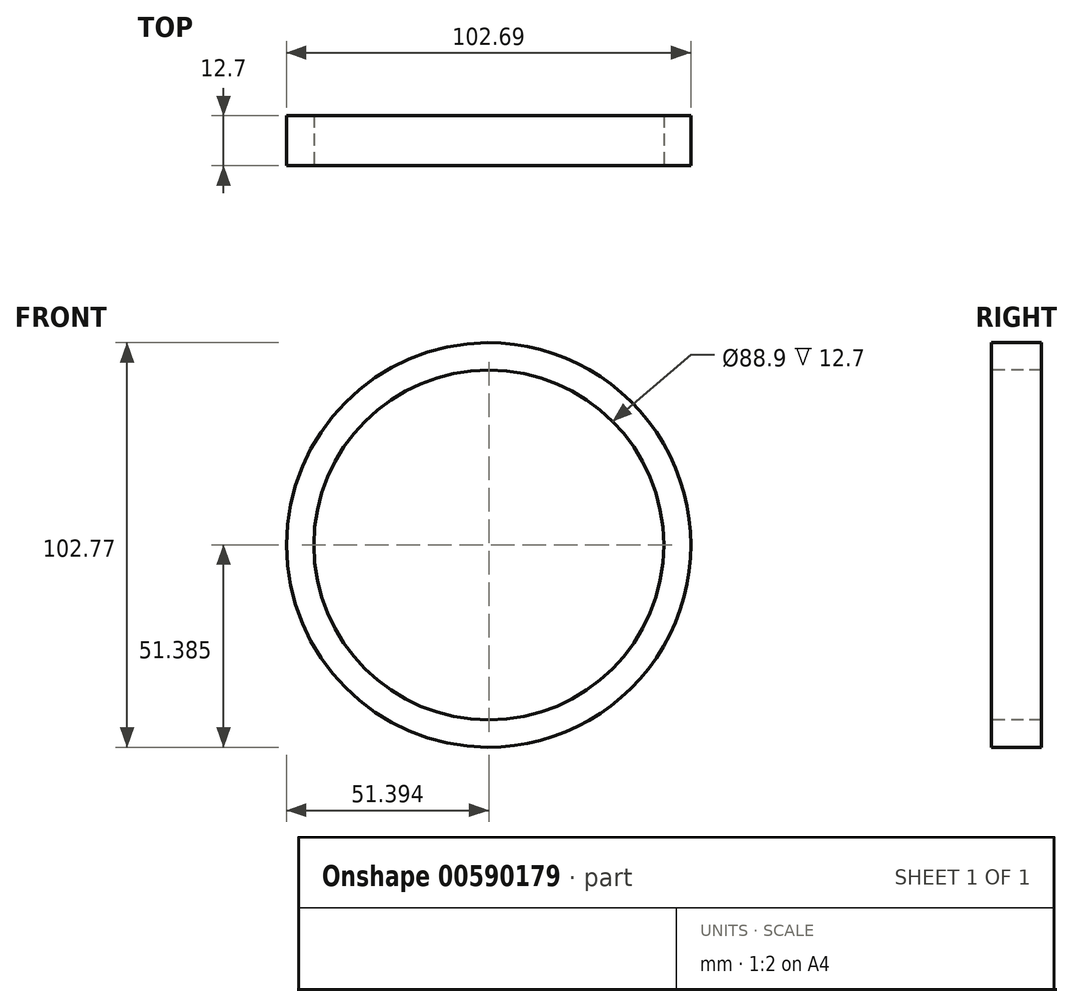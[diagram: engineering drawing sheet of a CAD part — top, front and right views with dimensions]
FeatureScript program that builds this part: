
annotation { "Feature Type Name" : "Feature", "Feature Type Description" : "" }
export const myFeature = defineFeature(function(context is Context, id is Id, definition is map)
    precondition{}
    {
        {
            var Q0;
            Q0=qCreatedBy(makeId("Front.planeOp"),FACE);
            var sketch = newSketch(context, id + "F0", { "sketchPlane" : qUnion([Q0])});
            skArc(sketch, "E0", {"start": v(6.6, -58.28) * mm, "mid": v(58.2, -6.9) * mm, "end": v(6.6, 44.5) * mm});
            skArc(sketch, "E1", {"start": v(6.6, 44.5) * mm, "mid": v(-44.49, -6.9) * mm, "end": v(6.6, -58.28) * mm});
            skSolve(sketch);
        }
        {
            var Q0;
            Q0 = qSketchRegion(id + "F0", true);
            extrude(context, id + "F1", {"entities" : qUnion([Q0]), "depth" : 12.7 * mm, "offsetDistance" : 25.4 * mm});
        }
        {
            var Q0;
            Q0=makeQuery(id+"F1.opExtrude","CAP_FACE",FACE,{"disambiguationData":[OSD([sQuery(id+"F0.wireOp",EDGE,"E0"),sQuery(id+"F0.wireOp",EDGE,"E1")])],"isStart":false});
            var sketch = newSketch(context, id + "F2", { "sketchPlane" : qUnion([Q0])});
            skCircle(sketch, "E2", {"center": v(6.9, -6.9) * mm, "radius": 44.45 * mm});
            skSolve(sketch);
        }
        {
            var Q0;
            Q0 = qSketchRegion(id + "F2", true);
            extrude(context, id + "F3", {"entities" : qUnion([Q0]), "operationType" : NewBodyOperationType.REMOVE, "oppositeDirection" : true, "depth" : 25.4 * mm, "offsetDistance" : 25.4 * mm});
        }
    });
